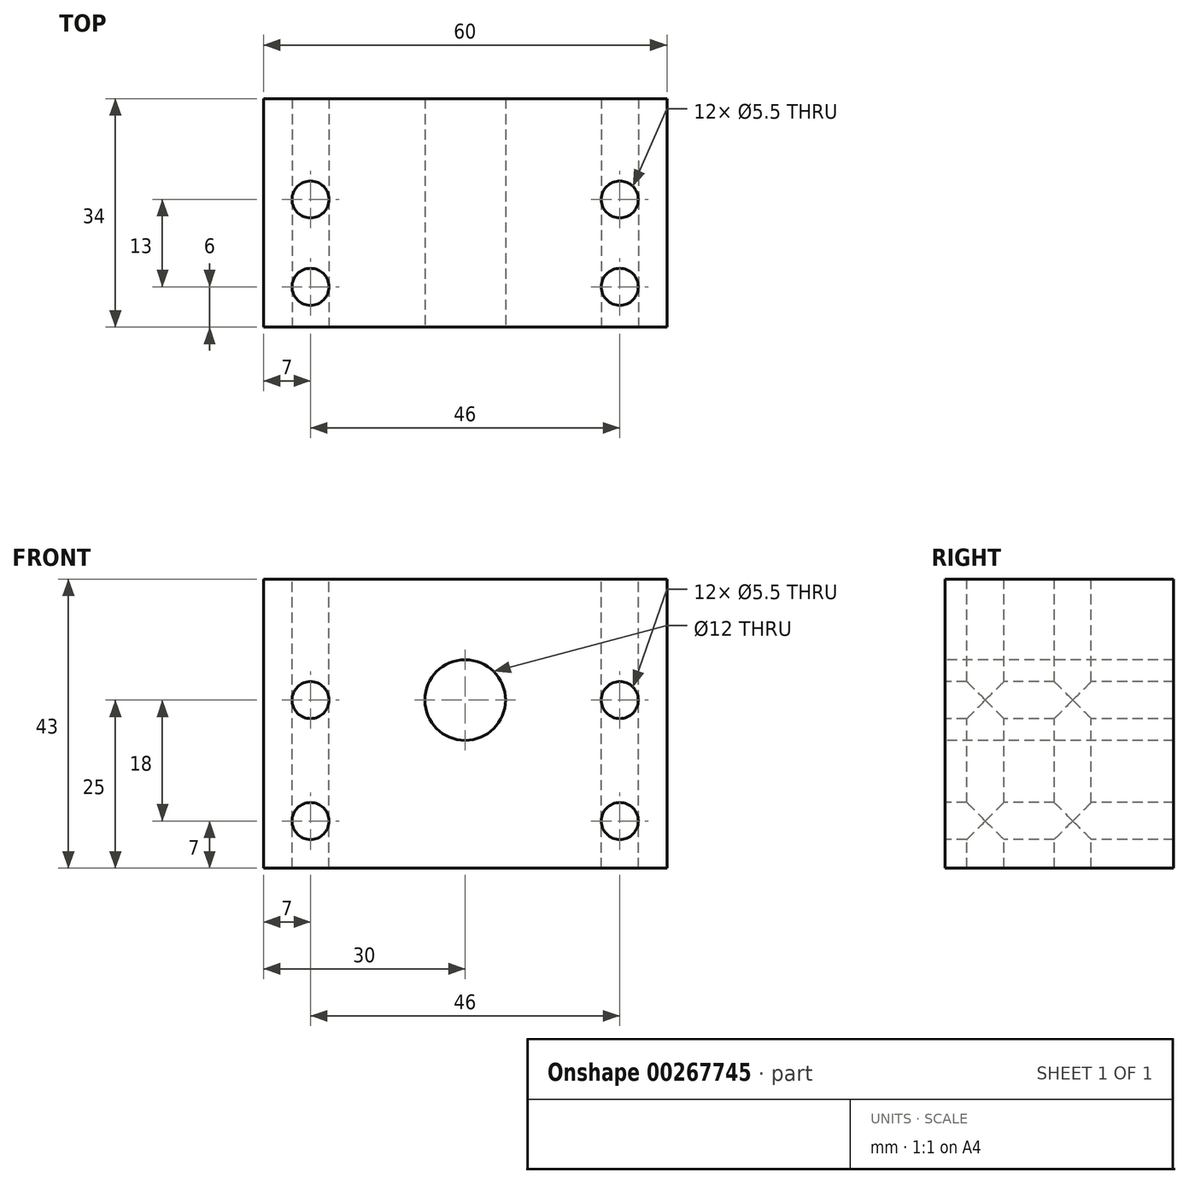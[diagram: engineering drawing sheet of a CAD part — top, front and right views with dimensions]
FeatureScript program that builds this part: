
annotation { "Feature Type Name" : "Feature", "Feature Type Description" : "" }
export const myFeature = defineFeature(function(context is Context, id is Id, definition is map)
    precondition{}
    {
        {
            var Q0;
            Q0=qCreatedBy(makeId("Front.planeOp"),FACE);
            var sketch = newSketch(context, id + "F0", { "sketchPlane" : qUnion([Q0])});
            skLineSegment(sketch, "E0.bottom", {"start": v(30, 21.5) * mm, "end": v(-30, 21.5) * mm});
            skLineSegment(sketch, "E0.top", {"start": v(30, -21.5) * mm, "end": v(-30, -21.5) * mm});
            skLineSegment(sketch, "E0.left", {"start": v(30, 21.5) * mm, "end": v(30, -21.5) * mm});
            skLineSegment(sketch, "E0.right", {"start": v(-30, 21.5) * mm, "end": v(-30, -21.5) * mm});
            skPoint(sketch, "E0.middle", {"position": v(0, 0) * mm});
            skLineSegment(sketch, "E1", {"start": v(0, -21.5) * mm, "end": v(0, 3.5) * mm, "construction": true});
            skCircle(sketch, "E2", {"center": v(0, 3.5) * mm, "radius": 6 * mm});
            skSolve(sketch);
        }
        {
            var Q0;
            Q0=makeQuery(id+"F0.imprint","IMPRINT",FACE,{"disambiguationData":[TD([[makeQuery(id+"F0.imprint","IMPRINT",EDGE,{"derivedFrom":sQuery(id+"F0.wireOp",EDGE,"E0.bottom")}),1.0]])]});
            extrude(context, id + "F1", {"entities" : qUnion([Q0]), "oppositeDirection" : true, "depth" : 34 * mm});
        }
        {
            var Q0;
            Q0=makeQuery(id+"F1.opExtrude","CAP_FACE",FACE,{"disambiguationData":[OSD([sQuery(id+"F0.wireOp",EDGE,"E0.bottom"),sQuery(id+"F0.wireOp",EDGE,"E0.top"),sQuery(id+"F0.wireOp",EDGE,"E0.left"),sQuery(id+"F0.wireOp",EDGE,"E0.right"),sQuery(id+"F0.wireOp",EDGE,"E2")])],"isStart":true});
            var sketch = newSketch(context, id + "F2", { "sketchPlane" : qUnion([Q0])});
            skLineSegment(sketch, "E3", {"start": v(-43.2, -21.5) * mm, "end": v(-43.2, 3.5) * mm, "construction": true});
            skLineSegment(sketch, "E4", {"start": v(-43.2, 3.5) * mm, "end": v(16.8, 3.5) * mm, "construction": true});
            skCircle(sketch, "E5", {"center": v(-23, 3.5) * mm, "radius": 2.75 * mm});
            skCircle(sketch, "E6", {"center": v(23, 3.5) * mm, "radius": 2.75 * mm});
            skLineSegment(sketch, "E7", {"start": v(0, -21.5) * mm, "end": v(0, 21.5) * mm, "construction": true});
            skLineSegment(sketch, "E8", {"start": v(-43.2, 3.5) * mm, "end": v(-43.2, -14.5) * mm, "construction": true});
            skLineSegment(sketch, "E9", {"start": v(-43.2, -14.5) * mm, "end": v(16.8, -14.5) * mm, "construction": true});
            skCircle(sketch, "E10", {"center": v(-23, -14.5) * mm, "radius": 2.75 * mm});
            skCircle(sketch, "E11", {"center": v(23, -14.5) * mm, "radius": 2.75 * mm});
            skSolve(sketch);
        }
        {
            var Q0;
            Q0=makeQuery(id+"F2.imprint","IMPRINT",FACE,{"disambiguationData":[TD([[makeQuery(id+"F2.imprint","IMPRINT",EDGE,{"derivedFrom":sQuery(id+"F2.wireOp",EDGE,"E6")}),1.0]])]});
            var Q1;
            Q1=makeQuery(id+"F2.imprint","IMPRINT",FACE,{"disambiguationData":[TD([[makeQuery(id+"F2.imprint","IMPRINT",EDGE,{"derivedFrom":sQuery(id+"F2.wireOp",EDGE,"E10")}),1.0]])]});
            var Q2;
            Q2=makeQuery(id+"F2.imprint","IMPRINT",FACE,{"disambiguationData":[TD([[makeQuery(id+"F2.imprint","IMPRINT",EDGE,{"derivedFrom":sQuery(id+"F2.wireOp",EDGE,"E11")}),1.0]])]});
            var Q3;
            Q3=makeQuery(id+"F2.imprint","IMPRINT",FACE,{"disambiguationData":[TD([[makeQuery(id+"F2.imprint","IMPRINT",EDGE,{"derivedFrom":sQuery(id+"F2.wireOp",EDGE,"E5")}),1.0]])]});
            extrude(context, id + "F3", {"entities" : qUnion([Q0, Q1, Q2, Q3]), "operationType" : NewBodyOperationType.REMOVE, "endBound" : BoundingType.THROUGH_ALL, "oppositeDirection" : true, "depth" : 25 * mm});
        }
        {
            var Q0;
            Q0=makeQuery(id+"F1.opExtrude","SWEPT_FACE",FACE,{"disambiguationData":[OSD([sQuery(id+"F0.wireOp",EDGE,"E0.bottom")])]});
            var sketch = newSketch(context, id + "F4", { "sketchPlane" : qUnion([Q0])});
            skLineSegment(sketch, "E12", {"start": v(0, 34) * mm, "end": v(-23, 34) * mm, "construction": true});
            skLineSegment(sketch, "E13", {"start": v(-23, 34) * mm, "end": v(-23, 0) * mm, "construction": true});
            skLineSegment(sketch, "E14", {"start": v(0, 34) * mm, "end": v(23, 34) * mm, "construction": true});
            skLineSegment(sketch, "E15", {"start": v(23, 34) * mm, "end": v(23, 0) * mm, "construction": true});
            skLineSegment(sketch, "E16", {"start": v(-30, 0) * mm, "end": v(-30, 19) * mm, "construction": true});
            skLineSegment(sketch, "E17", {"start": v(-30, 19) * mm, "end": v(30, 19) * mm, "construction": true});
            skLineSegment(sketch, "E18", {"start": v(30, 19) * mm, "end": v(30, 6) * mm, "construction": true});
            skLineSegment(sketch, "E19", {"start": v(30, 6) * mm, "end": v(-23, 6) * mm, "construction": true});
            skCircle(sketch, "E20", {"center": v(-23, 6) * mm, "radius": 2.75 * mm});
            skCircle(sketch, "E21", {"center": v(-23, 19) * mm, "radius": 2.75 * mm});
            skCircle(sketch, "E22", {"center": v(23, 19) * mm, "radius": 2.75 * mm});
            skCircle(sketch, "E23", {"center": v(23, 6) * mm, "radius": 2.75 * mm});
            skSolve(sketch);
        }
        {
            var Q0;
            Q0=makeQuery(id+"F4.imprint","IMPRINT",FACE,{"disambiguationData":[TD([[makeQuery(id+"F4.imprint","IMPRINT",EDGE,{"derivedFrom":sQuery(id+"F4.wireOp",EDGE,"E21")}),1.0]])]});
            var Q1;
            Q1=makeQuery(id+"F4.imprint","IMPRINT",FACE,{"disambiguationData":[TD([[makeQuery(id+"F4.imprint","IMPRINT",EDGE,{"derivedFrom":sQuery(id+"F4.wireOp",EDGE,"E20")}),1.0]])]});
            var Q2;
            Q2=makeQuery(id+"F4.imprint","IMPRINT",FACE,{"disambiguationData":[TD([[makeQuery(id+"F4.imprint","IMPRINT",EDGE,{"derivedFrom":sQuery(id+"F4.wireOp",EDGE,"E23")}),1.0]])]});
            var Q3;
            Q3=makeQuery(id+"F4.imprint","IMPRINT",FACE,{"disambiguationData":[TD([[makeQuery(id+"F4.imprint","IMPRINT",EDGE,{"derivedFrom":sQuery(id+"F4.wireOp",EDGE,"E22")}),1.0]])]});
            extrude(context, id + "F5", {"entities" : qUnion([Q0, Q1, Q2, Q3]), "operationType" : NewBodyOperationType.REMOVE, "endBound" : BoundingType.THROUGH_ALL, "oppositeDirection" : true, "depth" : 25 * mm});
        }
    });
